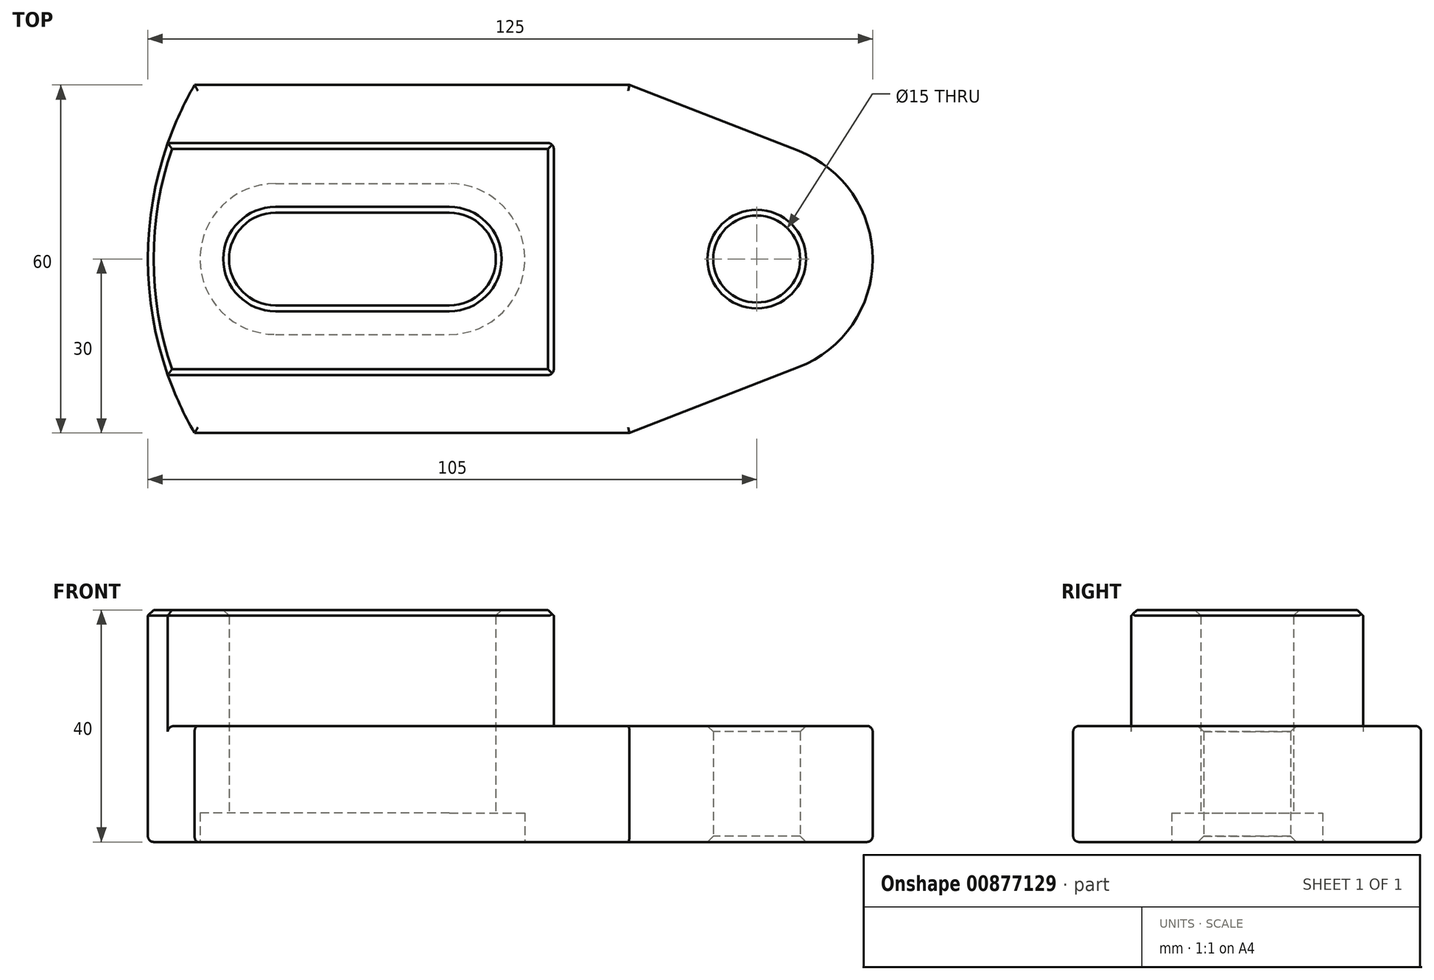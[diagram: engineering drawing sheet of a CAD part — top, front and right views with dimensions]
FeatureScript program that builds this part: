
annotation { "Feature Type Name" : "Feature", "Feature Type Description" : "" }
export const myFeature = defineFeature(function(context is Context, id is Id, definition is map)
    precondition{}
    {
        {
            var Q0;
            Q0=qCreatedBy(makeId("Top.planeOp"),FACE);
            var sketch = newSketch(context, id + "F0", { "sketchPlane" : qUnion([Q0])});
            skArc(sketch, "E0", {"start": v(-51.96, 30) * mm, "mid": v(-60, 0) * mm, "end": v(-51.96, -30) * mm});
            skCircle(sketch, "E1", {"center": v(45, 0) * mm, "radius": 7.5 * mm});
            skLineSegment(sketch, "E2", {"start": v(45, 0) * mm, "end": v(-50.55, 0) * mm, "construction": true});
            skArc(sketch, "E3", {"start": v(52.25, -18.64) * mm, "mid": v(65, 0) * mm, "end": v(52.25, 18.64) * mm});
            skLineSegment(sketch, "E4", {"start": v(-51.96, 30) * mm, "end": v(23.04, 30) * mm});
            skLineSegment(sketch, "E5.MirrorCS", {"start": v(-51.96, -30) * mm, "end": v(23.04, -30) * mm});
            skLineSegment(sketch, "E6", {"start": v(52.25, 18.64) * mm, "end": v(23.04, 30) * mm});
            skLineSegment(sketch, "E7.MirrorCS", {"start": v(52.25, -18.64) * mm, "end": v(23.04, -30) * mm});
            skArc(sketch, "E8", {"start": v(-8, -8) * mm, "mid": v(0, 0) * mm, "end": v(-8, 8) * mm});
            skArc(sketch, "E9", {"start": v(-38, 8) * mm, "mid": v(-46, 0) * mm, "end": v(-38, -8) * mm});
            skLineSegment(sketch, "E10", {"start": v(-38, 8) * mm, "end": v(-8, 8) * mm});
            skLineSegment(sketch, "E11.MirrorCS", {"start": v(-38, -8) * mm, "end": v(-8, -8) * mm});
            skSolve(sketch);
        }
        {
            var Q0;
            Q0 = qSketchRegion(id + "F0", true);
            extrude(context, id + "F1", {"entities" : qUnion([Q0]), "depth" : 20 * mm, "offsetDistance" : 25 * mm});
        }
        {
            var Q0;
            Q0=makeQuery(id+"F1.opExtrude","CAP_FACE",FACE,{"disambiguationData":[OSD([sQuery(id+"F0.wireOp",EDGE,"E0"),sQuery(id+"F0.wireOp",EDGE,"E1"),sQuery(id+"F0.wireOp",EDGE,"E3"),sQuery(id+"F0.wireOp",EDGE,"E4"),sQuery(id+"F0.wireOp",EDGE,"E5.MirrorCS"),sQuery(id+"F0.wireOp",EDGE,"E6"),sQuery(id+"F0.wireOp",EDGE,"E7.MirrorCS"),sQuery(id+"F0.wireOp",EDGE,"E8"),sQuery(id+"F0.wireOp",EDGE,"E9"),sQuery(id+"F0.wireOp",EDGE,"E10"),sQuery(id+"F0.wireOp",EDGE,"E11.MirrorCS")])],"isStart":false});
            var sketch = newSketch(context, id + "F2", { "sketchPlane" : qUnion([Q0])});
            skArc(sketch, "E12.0", {"start": v(-56.57, 20) * mm, "mid": v(-60, 0) * mm, "end": v(-56.57, -20) * mm});
            skLineSegment(sketch, "E13", {"start": v(0, 0) * mm, "end": v(-72.68, 0) * mm, "construction": true});
            skPoint(sketch, "E13.endSnap0", {"position": v(-60, 0) * mm});
            skLineSegment(sketch, "E14", {"start": v(-56.57, 20) * mm, "end": v(10, 20) * mm});
            skLineSegment(sketch, "E15.MirrorCS", {"start": v(-56.57, -20) * mm, "end": v(10, -20) * mm});
            skLineSegment(sketch, "E16", {"start": v(10, 20) * mm, "end": v(10, -20) * mm});
            skArc(sketch, "E17.0", {"start": v(-38, 8) * mm, "mid": v(-46, 0) * mm, "end": v(-38, -8) * mm});
            skLineSegment(sketch, "E17.1", {"start": v(-38, 8) * mm, "end": v(-8, 8) * mm});
            skArc(sketch, "E17.2", {"start": v(-8, -8) * mm, "mid": v(0, 0) * mm, "end": v(-8, 8) * mm});
            skLineSegment(sketch, "E17.3", {"start": v(-38, -8) * mm, "end": v(-8, -8) * mm});
            skSolve(sketch);
        }
        {
            var Q0;
            Q0 = qSketchRegion(id + "F2", true);
            extrude(context, id + "F3", {"entities" : qUnion([Q0]), "operationType" : NewBodyOperationType.ADD, "depth" : 20 * mm, "offsetDistance" : 25 * mm});
        }
        {
            var Q0;
            Q0=makeQuery(id+"F1.opExtrude","CAP_FACE",FACE,{"disambiguationData":[OSD([sQuery(id+"F0.wireOp",EDGE,"E0"),sQuery(id+"F0.wireOp",EDGE,"E1"),sQuery(id+"F0.wireOp",EDGE,"E3"),sQuery(id+"F0.wireOp",EDGE,"E4"),sQuery(id+"F0.wireOp",EDGE,"E5.MirrorCS"),sQuery(id+"F0.wireOp",EDGE,"E6"),sQuery(id+"F0.wireOp",EDGE,"E7.MirrorCS"),sQuery(id+"F0.wireOp",EDGE,"E8"),sQuery(id+"F0.wireOp",EDGE,"E9"),sQuery(id+"F0.wireOp",EDGE,"E10"),sQuery(id+"F0.wireOp",EDGE,"E11.MirrorCS")])],"isStart":true});
            var sketch = newSketch(context, id + "F4", { "sketchPlane" : qUnion([Q0])});
            skLineSegment(sketch, "E18.0", {"start": v(-38, 13) * mm, "end": v(-8, 13) * mm});
            skArc(sketch, "E18.1", {"start": v(-38, -13) * mm, "mid": v(-51, 0) * mm, "end": v(-38, 13) * mm});
            skLineSegment(sketch, "E18.2", {"start": v(-38, -13) * mm, "end": v(-8, -13) * mm});
            skArc(sketch, "E18.3", {"start": v(-8, 13) * mm, "mid": v(5, 0) * mm, "end": v(-8, -13) * mm});
            skSolve(sketch);
        }
        {
            var Q0;
            Q0 = qSketchRegion(id + "F4", true);
            extrude(context, id + "F5", {"entities" : qUnion([Q0]), "operationType" : NewBodyOperationType.REMOVE, "oppositeDirection" : true, "depth" : 5 * mm, "offsetDistance" : 25 * mm});
        }
        {
            var Q0;
            Q0=makeQuery(id+"F3.opExtrude","CAP_EDGE",EDGE,{"disambiguationData":[OSD([sQuery(id+"F2.wireOp",EDGE,"E15.MirrorCS")])],"isStart":false});
            var Q1;
            Q1=makeQuery(id+"F3.opExtrude","CAP_EDGE",EDGE,{"disambiguationData":[OSD([sQuery(id+"F2.wireOp",EDGE,"E12.0")])],"isStart":false});
            var Q2;
            Q2=makeQuery(id+"F3.opExtrude","CAP_FACE",FACE,{"disambiguationData":[OSD([sQuery(id+"F2.wireOp",EDGE,"E12.0"),sQuery(id+"F2.wireOp",EDGE,"E14"),sQuery(id+"F2.wireOp",EDGE,"E15.MirrorCS"),sQuery(id+"F2.wireOp",EDGE,"E16"),sQuery(id+"F2.wireOp",EDGE,"E17.0"),sQuery(id+"F2.wireOp",EDGE,"E17.1"),sQuery(id+"F2.wireOp",EDGE,"E17.2"),sQuery(id+"F2.wireOp",EDGE,"E17.3")])],"isStart":false});
            var Q3;
            Q3=makeQuery(id+"F1.opExtrude","CAP_EDGE",EDGE,{"disambiguationData":[OSD([sQuery(id+"F0.wireOp",EDGE,"E1")])],"isStart":false});
            chamfer(context, id + "F6", {"entities" : qUnion([Q0, Q1, Q2, Q3]), "width" : 1 * mm, "tangentPropagation" : true});
        }
        {
            var Q0;
            Q0=makeQuery(id+"F1.opExtrude","CAP_EDGE",EDGE,{"disambiguationData":[OSD([sQuery(id+"F0.wireOp",EDGE,"E5.MirrorCS")])],"isStart":false});
            var Q1;
            Q1=makeQuery(id+"F1.opExtrude","CAP_EDGE",EDGE,{"disambiguationData":[OSD([sQuery(id+"F0.wireOp",EDGE,"E7.MirrorCS")])],"isStart":false});
            var Q2;
            Q2=makeQuery(id+"F1.opExtrude","CAP_EDGE",EDGE,{"disambiguationData":[OSD([sQuery(id+"F0.wireOp",EDGE,"E5.MirrorCS")])],"isStart":true});
            var Q3;
            Q3=makeQuery(id+"F1.opExtrude","CAP_EDGE",EDGE,{"disambiguationData":[OSD([sQuery(id+"F0.wireOp",EDGE,"E7.MirrorCS")])],"isStart":true});
            var Q4;
            Q4=makeQuery(id+"F1.opExtrude","CAP_EDGE",EDGE,{"disambiguationData":[OSD([sQuery(id+"F0.wireOp",EDGE,"E4")])],"isStart":false});
            var Q5;
            Q5=makeQuery(id+"F1.opExtrude","CAP_EDGE",EDGE,{"disambiguationData":[OSD([sQuery(id+"F0.wireOp",EDGE,"E4")])],"isStart":true});
            var Q6;
            Q6=makeQuery(id+"F1.opExtrude","CAP_EDGE",EDGE,{"disambiguationData":[OSD([sQuery(id+"F0.wireOp",EDGE,"E0")])],"isStart":true});
            var Q7;
            {var subQ0=sQuery(id+"F0.wireOp",EDGE,"E4");var subQ1=sQuery(id+"F0.wireOp",EDGE,"E0");Q7=makeQuery(id+"F3.boolean.opBoolean","SPLIT",EDGE,{"disambiguationData":[TD([makeQuery(id+"F1.opExtrude","SWEPT_FACE",FACE,{"disambiguationData":[OSD([subQ0])]})])],"derivedFrom":makeQuery(id+"F1.opExtrude","CAP_EDGE",EDGE,{"disambiguationData":[OSD([subQ1])],"isStart":false})});}
            var Q8;
            {var subQ0=sQuery(id+"F0.wireOp",EDGE,"E5.MirrorCS");var subQ1=sQuery(id+"F0.wireOp",EDGE,"E0");Q8=makeQuery(id+"F3.boolean.opBoolean","SPLIT",EDGE,{"disambiguationData":[TD([makeQuery(id+"F1.opExtrude","SWEPT_FACE",FACE,{"disambiguationData":[OSD([subQ0])]})])],"derivedFrom":makeQuery(id+"F1.opExtrude","CAP_EDGE",EDGE,{"disambiguationData":[OSD([subQ1])],"isStart":false})});}
            var Q9;
            Q9=makeQuery(id+"F3.opExtrude","CAP_EDGE",EDGE,{"disambiguationData":[OSD([sQuery(id+"F2.wireOp",EDGE,"E15.MirrorCS")])],"isStart":true});
            var Q10;
            Q10=makeQuery(id+"F3.opExtrude","CAP_EDGE",EDGE,{"disambiguationData":[OSD([sQuery(id+"F2.wireOp",EDGE,"E16")])],"isStart":true});
            var Q11;
            Q11=makeQuery(id+"F3.opExtrude","SWEPT_EDGE",EDGE,{"disambiguationData":[OSD([sQuery(id+"F2.wireOp",EDGE,"E15.MirrorCS"),sQuery(id+"F2.wireOp",EDGE,"E16")])]});
            var Q12;
            Q12=makeQuery(id+"F3.opExtrude","SWEPT_EDGE",EDGE,{"disambiguationData":[OSD([sQuery(id+"F2.wireOp",EDGE,"E14"),sQuery(id+"F2.wireOp",EDGE,"E16")])]});
            fillet(context, id + "F7", {"entities" : qUnion([Q0, Q1, Q2, Q3, Q4, Q5, Q6, Q7, Q8, Q9, Q10, Q11, Q12]), "radius" : 1 * mm, "tangentPropagation" : true, "allowEdgeOverflow" : false});
        }
        {
            var Q0;
            Q0=makeQuery(id+"F1.opExtrude","CAP_EDGE",EDGE,{"disambiguationData":[OSD([sQuery(id+"F0.wireOp",EDGE,"E1")])],"isStart":true});
            var Q1;
            Q1=makeQuery(id+"F5.boolean.opBoolean","COPY",EDGE,{"derivedFrom":makeQuery(id+"F5.opExtrude","CAP_EDGE",EDGE,{"disambiguationData":[OSD([sQuery(id+"F4.wireOp",EDGE,"E18.3")])],"isStart":true})});
            chamfer(context, id + "F8", {"entities" : qUnion([Q0, Q1]), "width" : 1 * mm, "tangentPropagation" : true});
        }
    });
